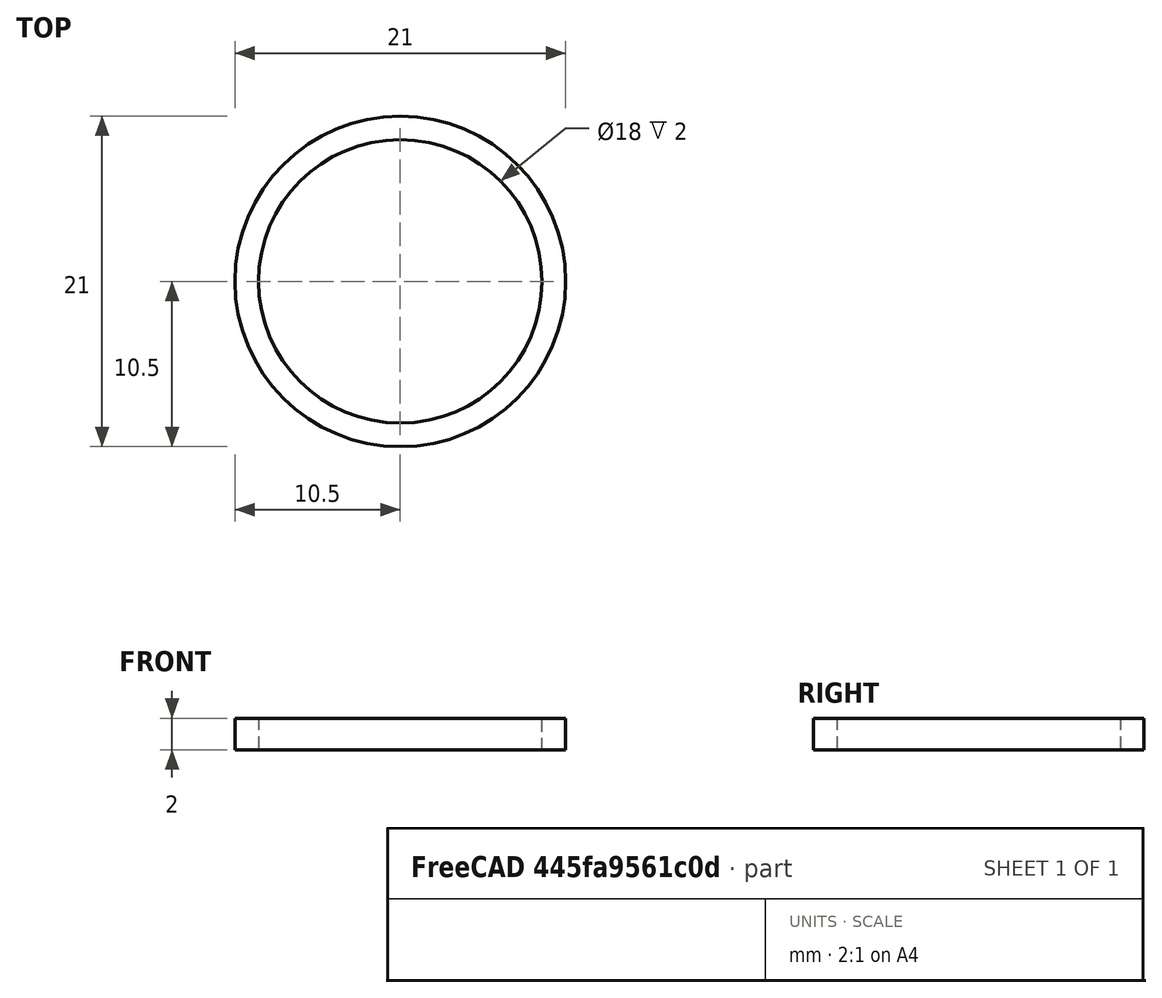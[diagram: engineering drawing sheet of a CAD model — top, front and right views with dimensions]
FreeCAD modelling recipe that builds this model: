
FCSTD DOCUMENT  (FreeCAD 0.19R23964 (Git))
Label: anillo
License: Creative Commons Attribution-ShareAlike
LicenseURL: http://creativecommons.org/licenses/by-sa/4.0/
objects: Sketcher::SketchObject×1, PartDesign::Pad×1, PartDesign::Body×1
note: 4 computed .brp shape members not serialized (recipe doc carries the construction recipe); baked Part::Feature solids carry a one-line shape summary decoded from their .brp

FEATURE [Sketcher::SketchObject] Sketch  label="plano"
  FullyConstrained = true
  MapMode = 5
  Support = -> [XY_Plane]
  sketch-geometry (2):
    g0: Circle CenterX=0 CenterY=0 CenterZ=0 NormalX=0 NormalY=0 NormalZ=1 AngleXU=0 Radius=9
    g1: Circle CenterX=0 CenterY=0 CenterZ=0 NormalX=0 NormalY=0 NormalZ=1 AngleXU=0 Radius=10.5
  constraints (4):
    c: Coincident(g0,g-1)
    c: Coincident(g1,g0)
    c: Diameter(g0) = 18
    c: Diameter(g1) = 21
FEATURE [PartDesign::Pad] Pad  label="Extruir"
  Direction = (1,1,1)
  Length = 2
  Length2 = 100
  Profile = -> Sketch
  Refine = true
  Type = 0
FEATURE [PartDesign::Body] Body  label="Anillo"
  Group = -> [Sketch,Pad]
  Origin = -> Origin
  Tip = -> Pad
